# Revit family: НЕВАТОМ_Вентилятор VO с рамой, версия 2
name_source: partatom
category: Оборудование
revit_build: Autodesk Revit 2017 (Build: 20170118_1100(x64)
units: mm (PartAtom-declared; Revit-internal decimal feet)

## family parameters
Всегда вертикально = Нет
На основе рабочей плоскости = Нет
Общий = Нет
При загрузке вырезать с полостями = Нет
Размер круглого соединителя = Использовать диаметр
Тип детали = Нормальный
Точка расчета площади = Нет

## types (38) — shared parameters
ADSK_Единица измерения = шт.
ADSK_Завод-изготовитель = НЕВАТОМ
ADSK_Количество = 1
ADSK_Материал наименование = Оцинкованная сталь
ADSK_Наименование = Осевой вентилятор
ADSK_Напряжение = 380 В
ADSK_Полная мощность = 0 кВт
ADSK_Ток = 0 А
Hv = 126 мм
Nevatom_URL = https://t.me
zero-valued in all types: ADSK_Частота вращения вентилятора

## per-type parameters (varying)
| type | ADSK_Марка | ADSK_Размер_Высота | ADSK_Размер_Длина | ADSK_Размер_Ширина | D | D верх вент | D осн вент | D* | D1.1 | D1v | D2 | D2.1 | D2v | H | L | L1 | h | А |
| VO № 4,0(63-90) | VO-4,5-О-2 | 505 мм | 480 мм | 490 мм | 400 мм | 50 мм | 80 мм | 33 мм | 293 мм | 373 мм | 480 мм | 187 мм | 267 мм | 505 мм | 420 мм | 490 мм | 285 мм | 510 мм |
| VO № 4,0(100) | VO-4,5-О-2 | 505 мм | 480 мм | 584 мм | 400 мм | 50 мм | 80 мм | 33 мм | 293 мм | 373 мм | 480 мм | 187 мм | 267 мм | 505 мм | 494 мм | 584 мм | 285 мм | 510 мм |
| VO № 5,0(63-80) | VO-5,0-О-2 | 625 мм | 560 мм | 540 мм | 500 мм | 63 мм | 100 мм | 42 мм | 367 мм | 467 мм | 560 мм | 233 мм | 333 мм | 625 мм | 450 мм | 540 мм | 350 мм | 610 мм |
| VO № 4,5(100) | VO-4,5-О-2 | 565 мм | 500 мм | 584 мм | 450 мм | 56 мм | 90 мм | 38 мм | 330 мм | 420 мм | 500 мм | 210 мм | 300 мм | 565 мм | 494 мм | 584 мм | 315 мм | 560 мм |
| VO № 5,0(90-112) | VO-5,0-О-2 | 625 мм | 560 мм | 584 мм | 500 мм | 63 мм | 100 мм | 42 мм | 367 мм | 467 мм | 560 мм | 233 мм | 333 мм | 625 мм | 494 мм | 584 мм | 350 мм | 610 мм |
| VO № 5,6(63 – 80, 90L4) | VO-5,6-О-2 | 695 мм | 620 мм | 550 мм | 560 мм | 70 мм | 112 мм | 47 мм | 411 мм | 523 мм | 620 мм | 261 мм | 373 мм | 695 мм | 450 мм | 550 мм | 410 мм | 670 мм |
| VO № 5,6(90L2, 100 – 112) | VO-5,6-О-2 | 695 мм | 620 мм | 594 мм | 560 мм | 70 мм | 112 мм | 47 мм | 411 мм | 523 мм | 620 мм | 261 мм | 373 мм | 695 мм | 494 мм | 594 мм | 410 мм | 670 мм |
| VO № 5,6(132) | VO-5,6-О-2 | 695 мм | 620 мм | 700 мм | 560 мм | 70 мм | 112 мм | 47 мм | 411 мм | 523 мм | 620 мм | 261 мм | 373 мм | 695 мм | 576 мм | 700 мм | 410 мм | 670 мм |
| VO № 5,6(160) | VO-5,6-О-2 | 695 мм | 620 мм | 860 мм | 560 мм | 70 мм | 112 мм | 47 мм | 411 мм | 523 мм | 620 мм | 261 мм | 373 мм | 695 мм | 720 мм | 860 мм | 410 мм | 670 мм |
| VO № 6,3(71 – 80, 90L4) | VO-6,3-О-2 | 785 мм | 690 мм | 560 мм | 630 мм | 79 мм | 126 мм | 53 мм | 462 мм | 588 мм | 690 мм | 294 мм | 420 мм | 785 мм | 450 мм | 560 мм | 445 мм | 740 мм |
| VO № 6,3(90L2, 100 – 112) | VO-6,3-О-2 | 785 мм | 690 мм | 594 мм | 630 мм | 79 мм | 126 мм | 53 мм | 462 мм | 588 мм | 690 мм | 294 мм | 420 мм | 785 мм | 494 мм | 594 мм | 445 мм | 740 мм |
| VO № 6,3(132) | VO-6,3-О-2 | 785 мм | 690 мм | 700 мм | 630 мм | 79 мм | 126 мм | 53 мм | 462 мм | 588 мм | 690 мм | 294 мм | 420 мм | 785 мм | 576 мм | 700 мм | 445 мм | 740 мм |
| VO № 7,1(71 – 90) | VO-7,1-О-2 | 875 мм | 770 мм | 574 мм | 710 мм | 89 мм | 142 мм | 59 мм | 521 мм | 663 мм | 770 мм | 331 мм | 473 мм | 875 мм | 450 мм | 574 мм | 495 мм | 820 мм |
| VO № 7,1(100 – 112) | VO-7,1-О-2 | 875 мм | 770 мм | 594 мм | 710 мм | 89 мм | 142 мм | 59 мм | 521 мм | 663 мм | 770 мм | 331 мм | 473 мм | 875 мм | 494 мм | 594 мм | 495 мм | 820 мм |
| VO № 7,1(132) | VO-7,1-О-2 | 875 мм | 770 мм | 700 мм | 710 мм | 89 мм | 142 мм | 59 мм | 521 мм | 663 мм | 770 мм | 331 мм | 473 мм | 875 мм | 576 мм | 700 мм | 495 мм | 820 мм |
| VO № 7,1(160) | VO-7,1-О-2 | 875 мм | 770 мм | 860 мм | 710 мм | 89 мм | 142 мм | 59 мм | 521 мм | 663 мм | 770 мм | 331 мм | 473 мм | 875 мм | 720 мм | 860 мм | 495 мм | 820 мм |
| VO № 8,0(71 – 90) | VO-9,0-О-2 | 980 мм | 860 мм | 590 мм | 800 мм | 100 мм | 160 мм | 67 мм | 587 мм | 747 мм | 860 мм | 373 мм | 533 мм | 980 мм | 450 мм | 590 мм | 550 мм | 910 мм |
| VO № 8,0(100 – 112) | VO-8,0-О-2 | 980 мм | 860 мм | 594 мм | 800 мм | 100 мм | 160 мм | 67 мм | 587 мм | 747 мм | 860 мм | 373 мм | 533 мм | 980 мм | 494 мм | 594 мм | 550 мм | 910 мм |
| VO № 8,0(132) | VO-8,0-О-2 | 980 мм | 860 мм | 740 мм | 800 мм | 100 мм | 160 мм | 67 мм | 587 мм | 747 мм | 860 мм | 373 мм | 533 мм | 980 мм | 600 мм | 740 мм | 550 мм | 910 мм |
| VO № 8,0(160) | VO-8,0-О-2 | 980 мм | 860 мм | 860 мм | 800 мм | 100 мм | 160 мм | 67 мм | 587 мм | 747 мм | 860 мм | 373 мм | 533 мм | 980 мм | 720 мм | 860 мм | 550 мм | 910 мм |
| VO № 9,0(71 – 90) | VO-9,0-О-2 | 1105 мм | 970 мм | 492 мм | 900 мм | 113 мм | 180 мм | 75 мм | 660 мм | 840 мм | 970 мм | 420 мм | 600 мм | 1105 мм | 450 мм | 492 мм | 605 мм | 1010 мм |
| VO № 9,0(100) | VO-9,0-0-2 | 1105 мм | 970 мм | 562 мм | 900 мм | 113 мм | 180 мм | 75 мм | 660 мм | 840 мм | 970 мм | 420 мм | 600 мм | 1105 мм | 520 мм | 562 мм | 605 мм | 1010 мм |
| VO № 9,0(112 – 132) | VO-9,0-О-2 | 1105 мм | 970 мм | 672 мм | 900 мм | 113 мм | 180 мм | 75 мм | 660 мм | 840 мм | 970 мм | 420 мм | 600 мм | 1105 мм | 600 мм | 672 мм | 605 мм | 1010 мм |
| VO № 9,0(160) | VO-9,0-О-2 | 1105 мм | 970 мм | 792 мм | 900 мм | 113 мм | 180 мм | 75 мм | 660 мм | 840 мм | 970 мм | 420 мм | 600 мм | 1105 мм | 750 мм | 792 мм | 605 мм | 1010 мм |
| VO № 10(80 – 90) | VO-10,0-О-2 | 1210 мм | 1070 мм | 492 мм | 1000 мм | 125 мм | 200 мм | 83 мм | 733 мм | 933 мм | 1070 мм | 467 мм | 667 мм | 1210 мм | 450 мм | 492 мм | 675 мм | 1110 мм |
| VO № 10(100) | VO-10,0-О-2 | 1210 мм | 1070 мм | 562 мм | 1000 мм | 125 мм | 200 мм | 83 мм | 733 мм | 933 мм | 1070 мм | 467 мм | 667 мм | 1210 мм | 520 мм | 562 мм | 675 мм | 1110 мм |
| VO № 10(112 – 132) | VO-10,0-О-2 | 1210 мм | 1070 мм | 642 мм | 1000 мм | 125 мм | 200 мм | 83 мм | 733 мм | 933 мм | 1070 мм | 467 мм | 667 мм | 1210 мм | 600 мм | 642 мм | 675 мм | 1110 мм |
| VO № 10(160) | VO-10,0-О-2 | 1210 мм | 1070 мм | 842 мм | 1000 мм | 125 мм | 200 мм | 83 мм | 733 мм | 933 мм | 1070 мм | 467 мм | 667 мм | 1210 мм | 800 мм | 842 мм | 675 мм | 1110 мм |
| VO № 10(180) | VO-10,0-О-2 | 1210 мм | 1070 мм | 942 мм | 1000 мм | 125 мм | 200 мм | 83 мм | 733 мм | 933 мм | 1070 мм | 467 мм | 667 мм | 1210 мм | 900 мм | 942 мм | 675 мм | 1110 мм |
| VO № 11,2(80 – 90) | VO-11,0-О-2 | 1355 мм | 1190 мм | 506 мм | 1120 мм | 140 мм | 224 мм | 93 мм | 821 мм | 1045 мм | 1190 мм | 523 мм | 747 мм | 1355 мм | 450 мм | 506 мм | 750 мм | 1230 мм |
| VO № 11,2(100) | VO-11,0-О-2 | 1355 мм | 1190 мм | 556 мм | 1120 мм | 140 мм | 224 мм | 93 мм | 821 мм | 1045 мм | 1190 мм | 523 мм | 747 мм | 1355 мм | 520 мм | 556 мм | 750 мм | 1230 мм |
| VO № 11,2(112 – 132) | VO-11,0-О-2 | 1355 мм | 1190 мм | 643 мм | 1120 мм | 140 мм | 224 мм | 93 мм | 821 мм | 1045 мм | 1190 мм | 523 мм | 747 мм | 1355 мм | 600 мм | 643 мм | 750 мм | 1230 мм |
| VO № 11,2(160) | VO-11,0-О-2 | 1355 мм | 1190 мм | 843 мм | 1120 мм | 140 мм | 224 мм | 93 мм | 821 мм | 1045 мм | 1190 мм | 523 мм | 747 мм | 1355 мм | 800 мм | 843 мм | 750 мм | 1230 мм |
| VO № 11,2(180 – 200) | VO-11,0-О-2 | 1355 мм | 1190 мм | 943 мм | 1120 мм | 140 мм | 224 мм | 93 мм | 821 мм | 1045 мм | 1190 мм | 523 мм | 747 мм | 1355 мм | 900 мм | 943 мм | 750 мм | 1230 мм |
| VO № 12,5(90 – 100) | VO-12,5-О-2 | 1510 мм | 1320 мм | 506 мм | 1250 мм | 156 мм | 250 мм | 104 мм | 917 мм | 1167 мм | 1320 мм | 583 мм | 833 мм | 1510 мм | 480 мм | 506 мм | 850 мм | 1360 мм |
| VO № 12,5(112 – 132) | VO-12,5-О-2 | 1510 мм | 1320 мм | 626 мм | 1250 мм | 156 мм | 250 мм | 104 мм | 917 мм | 1167 мм | 1320 мм | 583 мм | 833 мм | 1510 мм | 600 мм | 626 мм | 850 мм | 1360 мм |
| VO № 12,5(160 – 180) | VO-12,5-О-2 | 1510 мм | 1320 мм | 876 мм | 1250 мм | 156 мм | 250 мм | 104 мм | 917 мм | 1167 мм | 1320 мм | 583 мм | 833 мм | 1510 мм | 850 мм | 876 мм | 850 мм | 1360 мм |
| VO № 12,5(200 – 250) | VO-12,5-О-2 | 1510 мм | 1320 мм | 1026 мм | 1250 мм | 156 мм | 250 мм | 104 мм | 917 мм | 1167 мм | 1320 мм | 583 мм | 833 мм | 1510 мм | 1000 мм | 1026 мм | 850 мм | 1360 мм |
